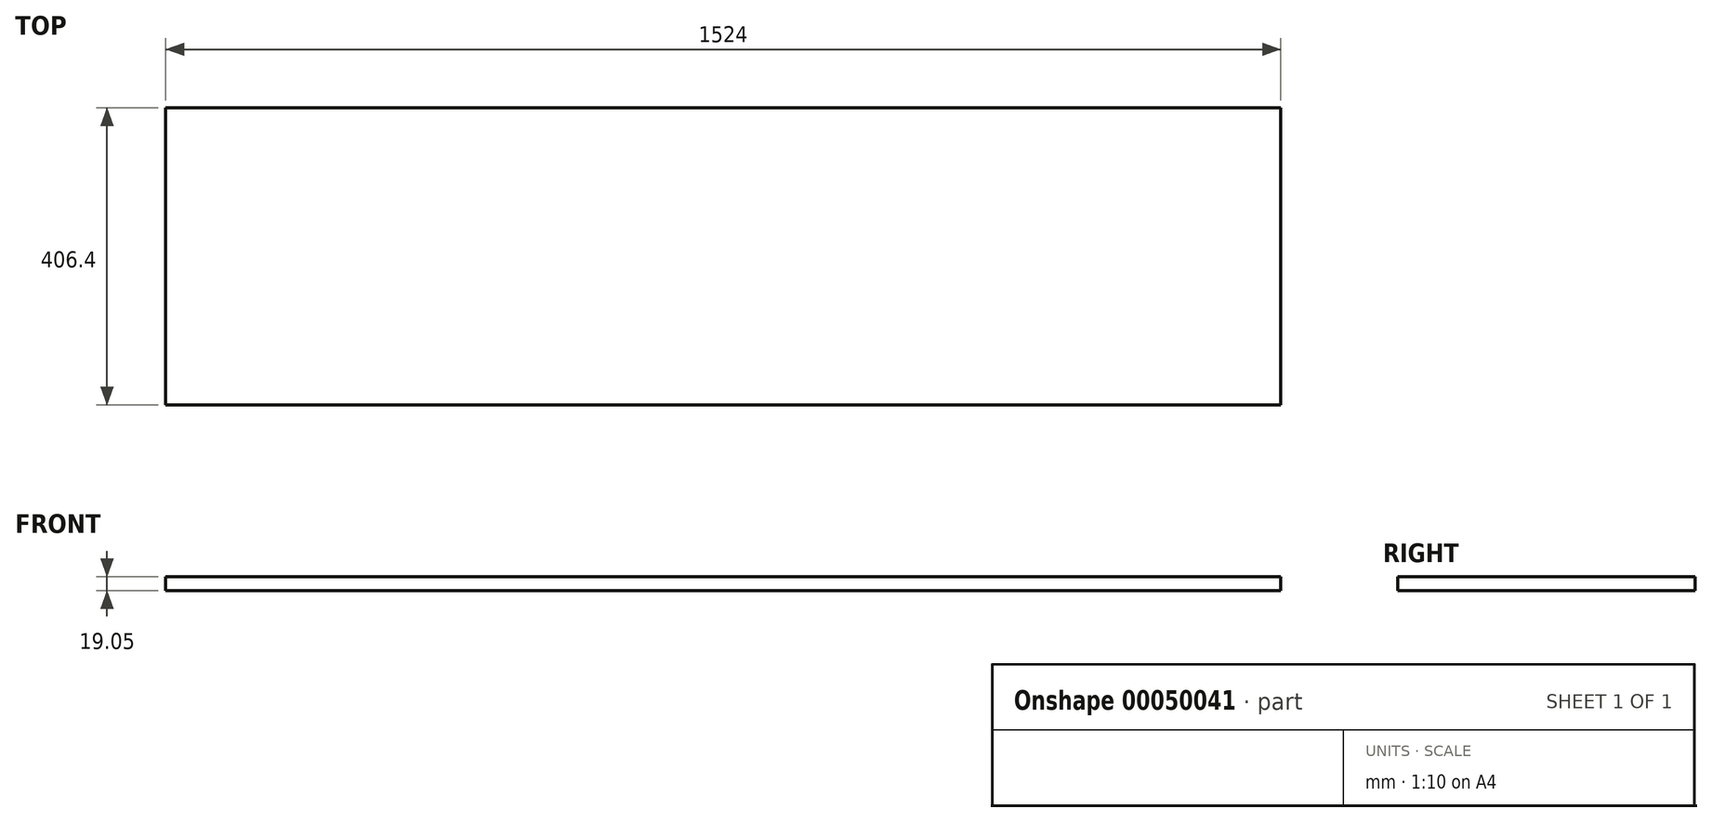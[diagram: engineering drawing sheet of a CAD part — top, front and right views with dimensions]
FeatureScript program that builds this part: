
annotation { "Feature Type Name" : "Feature", "Feature Type Description" : "" }
export const myFeature = defineFeature(function(context is Context, id is Id, definition is map)
    precondition{}
    {
        {
            var Q0;
            Q0=qCreatedBy(makeId("Top.planeOp"),FACE);
            var sketch = newSketch(context, id + "F0", { "sketchPlane" : qUnion([Q0])});
            skLineSegment(sketch, "E0.bottom", {"start": v(0, 0) * mm, "end": v(1524, 0) * mm});
            skLineSegment(sketch, "E0.top", {"start": v(0, 406.4) * mm, "end": v(1524, 406.4) * mm});
            skLineSegment(sketch, "E0.left", {"start": v(0, 0) * mm, "end": v(0, 406.4) * mm});
            skLineSegment(sketch, "E0.right", {"start": v(1524, 0) * mm, "end": v(1524, 406.4) * mm});
            skSolve(sketch);
        }
        {
            var Q0;
            Q0=makeQuery(id+"F0.imprint","IMPRINT",FACE,{"disambiguationData":[TD([[makeQuery(id+"F0.imprint","IMPRINT",EDGE,{"derivedFrom":sQuery(id+"F0.wireOp",EDGE,"E0.bottom")}),1.0]])]});
            extrude(context, id + "F1", {"entities" : qUnion([Q0]), "depth" : 19.05 * mm});
        }
    });
